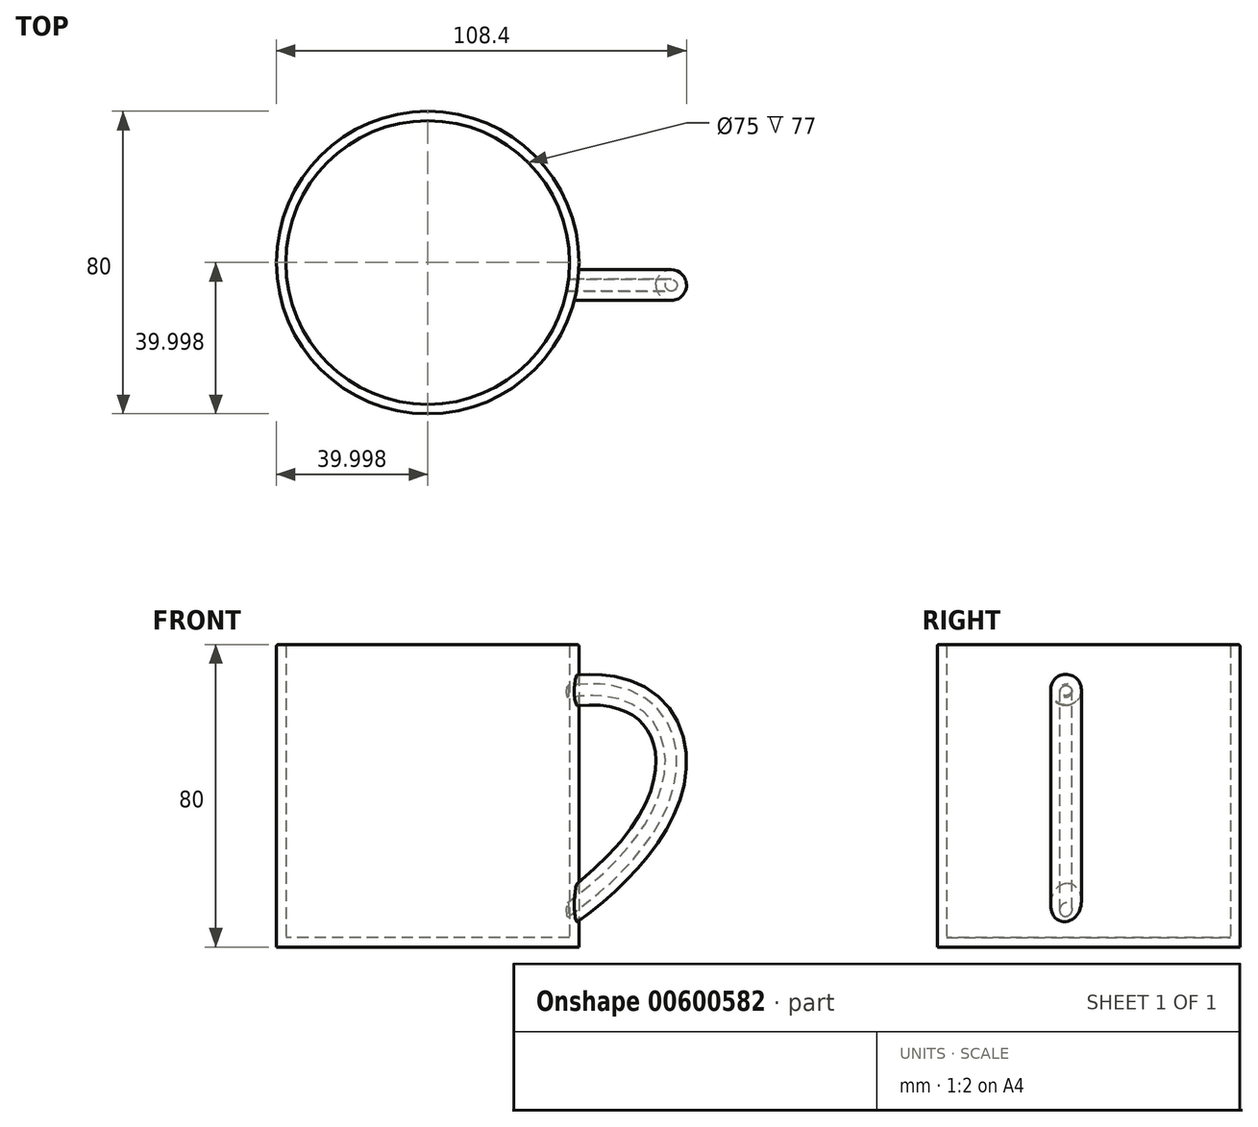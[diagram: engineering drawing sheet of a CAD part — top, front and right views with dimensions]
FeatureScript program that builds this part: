
annotation { "Feature Type Name" : "Feature", "Feature Type Description" : "" }
export const myFeature = defineFeature(function(context is Context, id is Id, definition is map)
    precondition{}
    {
        {
            var Q0;
            Q0=qCreatedBy(makeId("Top.planeOp"),FACE);
            var sketch = newSketch(context, id + "F0", { "sketchPlane" : qUnion([Q0])});
            skCircle(sketch, "E0", {"center": v(-12.08, 5.97) * mm, "radius": 40 * mm});
            skSolve(sketch);
        }
        {
            var Q0;
            Q0=makeQuery(id+"F0.imprint","IMPRINT",FACE,{"disambiguationData":[TD([[makeQuery(id+"F0.imprint","IMPRINT",EDGE,{"derivedFrom":sQuery(id+"F0.wireOp",EDGE,"E0")}),1.0]])]});
            extrude(context, id + "F1", {"entities" : qUnion([Q0]), "depth" : 80 * mm, "offsetDistance" : 25 * mm});
        }
        {
            var Q0;
            Q0=qCreatedBy(makeId("Front.planeOp"),FACE);
            var sketch = newSketch(context, id + "F2", { "sketchPlane" : qUnion([Q0])});
            skFitSpline(sketch, "E1", {"points": [v(22.27, 68.27) * mm, v(51.2, 58.66) * mm, v(25.47, 8.88) * mm], "startDerivative": vector(102.4, 20.53) * mm, "endDerivative": vector(-139.44, -99) * mm});
            skSolve(sketch);
        }
        {
            var Q0;
            Q0=qCreatedBy(makeId("Right.planeOp"),FACE);
            cPlane(context, id + "F3", {"entities" : qUnion([Q0]), "cplaneType" : CPlaneType.OFFSET, "offset" : 28.5 * mm, "width" : 150 * mm, "height" : 150 * mm});
        }
        {
            var Q0;
            Q0=qCreatedBy(id+"F3.planeOp",FACE);
            var sketch = newSketch(context, id + "F4", { "sketchPlane" : qUnion([Q0])});
            skCircle(sketch, "E2", {"center": v(0, 67.97) * mm, "radius": 4.06 * mm});
            skSolve(sketch);
        }
        {
            var Q0;
            Q0=makeQuery(id+"F4.imprint","IMPRINT",FACE,{"disambiguationData":[TD([[makeQuery(id+"F4.imprint","IMPRINT",EDGE,{"derivedFrom":sQuery(id+"F4.wireOp",EDGE,"E2")}),1.0]])]});
            var Q1;
            Q1=sQuery(id+"F2.wireOp",EDGE,"E1");
            sweep(context, id + "F5", {"operationType" : NewBodyOperationType.ADD, "profiles" : qUnion([Q0]), "path" : qUnion([Q1])});
        }
        {
            var Q0;
            Q0=makeQuery(id+"F1.opExtrude","CAP_FACE",FACE,{"disambiguationData":[OSD([sQuery(id+"F0.wireOp",EDGE,"E0")])],"isStart":false});
            shell(context, id + "F6", {"entities" : qUnion([Q0]), "thickness" : 2.5 * mm});
        }
        {
            var Q0;
            Q0=makeQuery(id+"F1.opExtrude","CAP_EDGE",EDGE,{"disambiguationData":[OSD([sQuery(id+"F0.wireOp",EDGE,"E0")])],"isStart":false});
            var Q1;
            {var subQ0=sQuery(id+"F0.wireOp",EDGE,"E0");Q1=makeQuery(id+"F6.opShell","OFFSET_EDGE",EDGE,{"disambiguationData":[OSD([subQ0]),TDD([makeQuery(id+"F1.opExtrude","CAP_EDGE",EDGE,{"disambiguationData":[OSD([subQ0])],"isStart":false})])]});}
            fillet(context, id + "F7", {"entities" : qUnion([Q0, Q1]), "radius" : 0.5 * mm, "tangentPropagation" : true, "allowEdgeOverflow" : false});
        }
    });
